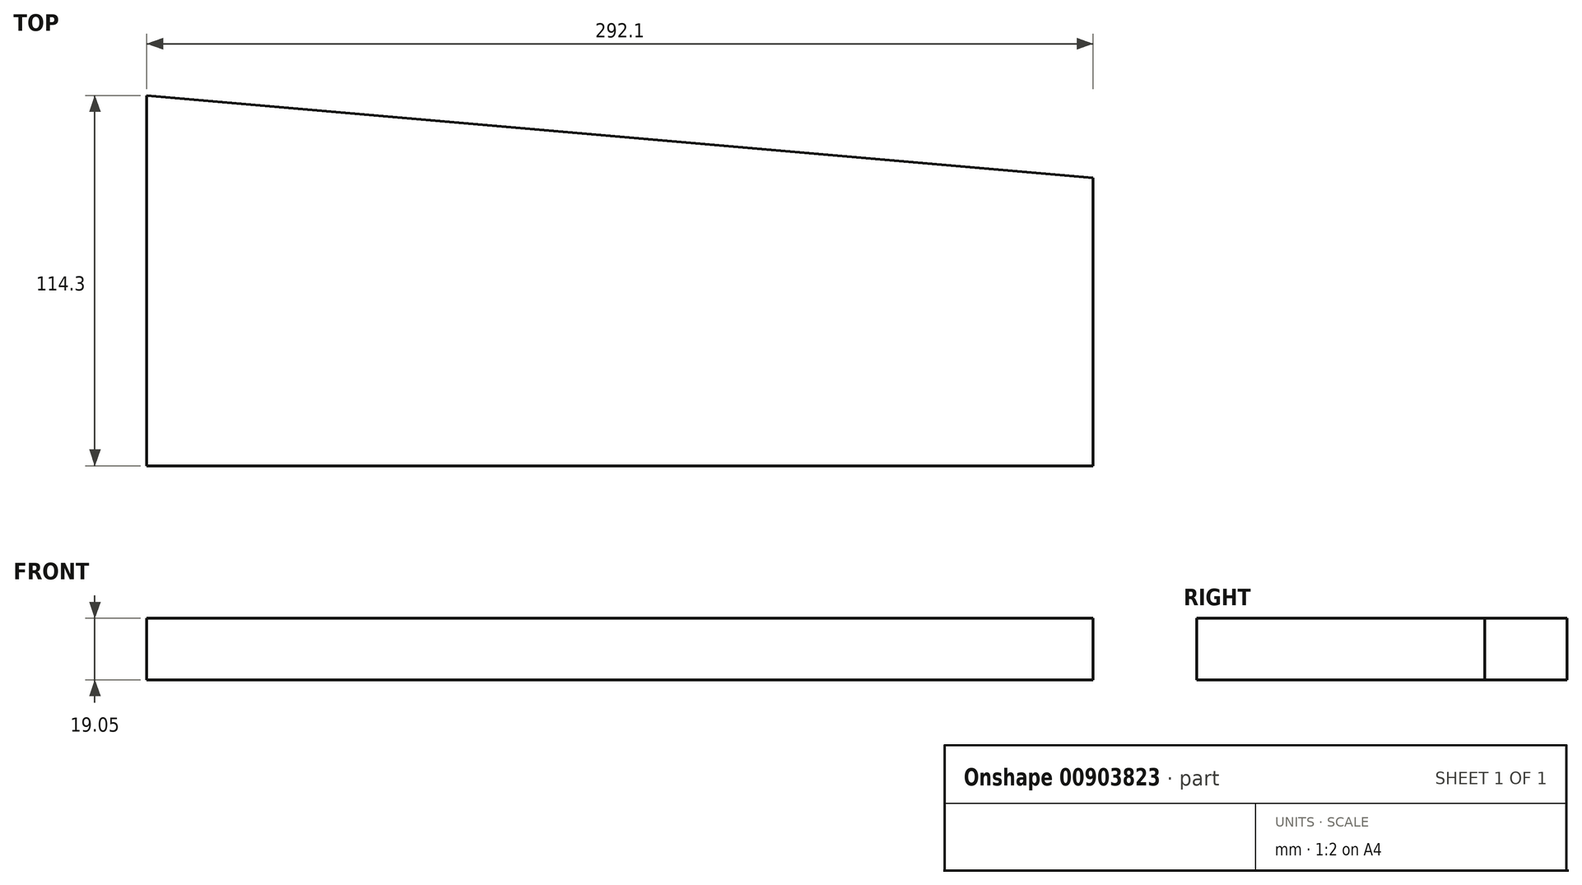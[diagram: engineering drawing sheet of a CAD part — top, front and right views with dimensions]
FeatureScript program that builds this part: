
annotation { "Feature Type Name" : "Feature", "Feature Type Description" : "" }
export const myFeature = defineFeature(function(context is Context, id is Id, definition is map)
    precondition{}
    {
        {
            var Q0;
            Q0=qCreatedBy(makeId("Top.planeOp"),FACE);
            var sketch = newSketch(context, id + "F0", { "sketchPlane" : qUnion([Q0])});
            skLineSegment(sketch, "E0.bottom", {"start": v(0, 0) * mm, "end": v(292.1, 0) * mm});
            skLineSegment(sketch, "E0.top", {"start": v(0, 114.3) * mm, "end": v(292.1, 114.3) * mm});
            skLineSegment(sketch, "E0.left", {"start": v(0, 0) * mm, "end": v(0, 114.3) * mm});
            skLineSegment(sketch, "E0.right", {"start": v(292.1, 0) * mm, "end": v(292.1, 114.3) * mm});
            skSolve(sketch);
        }
        {
            var Q0;
            Q0 = qSketchRegion(id + "F0", true);
            extrude(context, id + "F1", {"entities" : qUnion([Q0]), "depth" : 19.05 * mm, "offsetDistance" : 25.4 * mm});
        }
        {
            var Q0;
            Q0=makeQuery(id+"F1.opExtrude","CAP_FACE",FACE,{"disambiguationData":[OSD([sQuery(id+"F0.wireOp",EDGE,"E0.bottom"),sQuery(id+"F0.wireOp",EDGE,"E0.top"),sQuery(id+"F0.wireOp",EDGE,"E0.left"),sQuery(id+"F0.wireOp",EDGE,"E0.right")])],"isStart":false});
            var sketch = newSketch(context, id + "F2", { "sketchPlane" : qUnion([Q0])});
            skLineSegment(sketch, "E1", {"start": v(0, 114.3) * mm, "end": v(19.05, 114.3) * mm, "construction": true});
            skLineSegment(sketch, "E2", {"start": v(292.1, 0) * mm, "end": v(292.1, 88.9) * mm, "construction": true});
            skLineSegment(sketch, "E3", {"start": v(0, 114.3) * mm, "end": v(292.1, 88.9) * mm});
            skSolve(sketch);
        }
        {
            var Q0;
            Q0 = qSketchRegion(id + "F2", true);
            var Q1;
            {var subQ0=sQuery(id+"F2.wireOp",EDGE,"E3");Q1=makeQuery(id+"F2.imprint","IMPRINT",FACE,{"disambiguationData":[TD([[makeQuery(id+"F2.imprint","IMPRINT",EDGE,{"derivedFrom":subQ0}),1.0]])]});}
            extrude(context, id + "F3", {"entities" : qUnion([Q0, Q1]), "operationType" : NewBodyOperationType.REMOVE, "oppositeDirection" : true, "depth" : 25.4 * mm, "offsetDistance" : 25.4 * mm});
        }
    });
